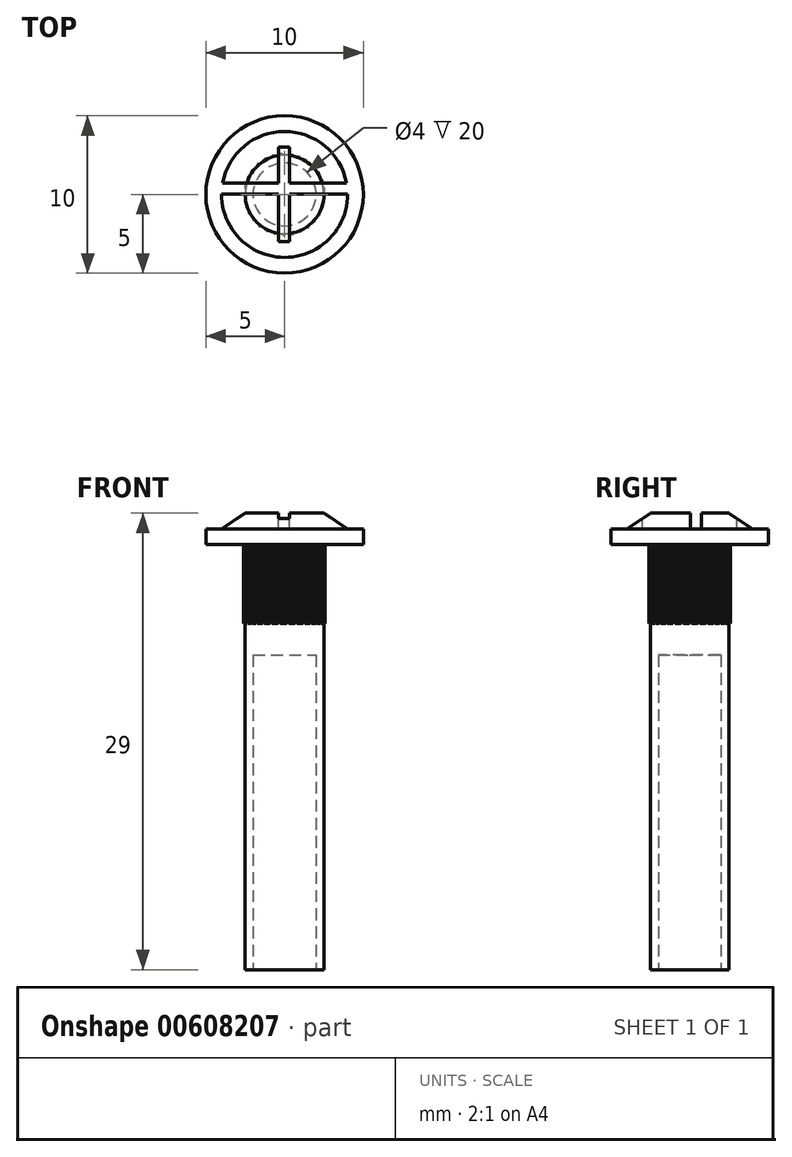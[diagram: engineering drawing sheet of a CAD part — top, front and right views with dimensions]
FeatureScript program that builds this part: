
annotation { "Feature Type Name" : "Feature", "Feature Type Description" : "" }
export const myFeature = defineFeature(function(context is Context, id is Id, definition is map)
    precondition{}
    {
        {
            var Q0;
            Q0=qCreatedBy(makeId("Front.planeOp"),FACE);
            var sketch = newSketch(context, id + "F0", { "sketchPlane" : qUnion([Q0])});
            skLineSegment(sketch, "E0.bottom", {"start": v(0, 12.5) * mm, "end": v(2.5, 12.5) * mm});
            skLineSegment(sketch, "E0.top", {"start": v(0, -14.5) * mm, "end": v(2.5, -14.5) * mm});
            skLineSegment(sketch, "E0.right", {"start": v(2.5, 12.5) * mm, "end": v(2.5, -14.5) * mm});
            skLineSegment(sketch, "E1", {"start": v(2.5, 14.5) * mm, "end": v(4, 13.5) * mm});
            skLineSegment(sketch, "E2", {"start": v(4, 13.5) * mm, "end": v(5, 13.5) * mm});
            skLineSegment(sketch, "E3", {"start": v(5, 13.5) * mm, "end": v(5, 12.5) * mm});
            skLineSegment(sketch, "E4", {"start": v(5, 12.5) * mm, "end": v(2.5, 12.5) * mm});
            skLineSegment(sketch, "E5", {"start": v(0, -14.5) * mm, "end": v(0, 14.5) * mm});
            skLineSegment(sketch, "E6", {"start": v(2.5, 14.5) * mm, "end": v(0, 14.5) * mm});
            skSolve(sketch);
        }
        {
            var Q0;
            Q0 = qSketchRegion(id + "F0", true);
            var Q1;
            Q1=sQuery(id+"F0.wireOp",EDGE,"E5");
            revolve(context, id + "F1", {"entities" : qUnion([Q0]), "axis" : qUnion([Q1]), "revolveType" : RevolveType.FULL});
        }
        {
            var Q0;
            Q0=makeQuery(id+"F1.opRevolve","SWEPT_FACE",FACE,{"disambiguationData":[OSD([sQuery(id+"F0.wireOp",EDGE,"E0.top")])]});
            var sketch = newSketch(context, id + "F2", { "sketchPlane" : qUnion([Q0])});
            skCircle(sketch, "E7", {"center": v(0, 0) * mm, "radius": 2 * mm});
            skSolve(sketch);
        }
        {
            var Q0;
            Q0 = qSketchRegion(id + "F2", true);
            extrude(context, id + "F3", {"entities" : qUnion([Q0]), "operationType" : NewBodyOperationType.REMOVE, "oppositeDirection" : true, "depth" : 20 * mm, "offsetDistance" : 25 * mm});
        }
        {
            var Q0;
            Q0=makeQuery(id+"F1.opRevolve","SWEPT_FACE",FACE,{"disambiguationData":[OSD([sQuery(id+"F0.wireOp",EDGE,"E6")])]});
            var sketch = newSketch(context, id + "F4", { "sketchPlane" : qUnion([Q0])});
            skLineSegment(sketch, "E8.bottom", {"start": v(-4, 0.73) * mm, "end": v(4, 0.73) * mm});
            skLineSegment(sketch, "E8.top", {"start": v(-4, 0.03) * mm, "end": v(4, 0.03) * mm});
            skLineSegment(sketch, "E8.left", {"start": v(-4, 0.73) * mm, "end": v(-4, 0.03) * mm});
            skLineSegment(sketch, "E8.right", {"start": v(4, 0.73) * mm, "end": v(4, 0.03) * mm});
            skLineSegment(sketch, "E9.bottom", {"start": v(-0.39, 3) * mm, "end": v(0.31, 3) * mm});
            skLineSegment(sketch, "E9.top", {"start": v(-0.39, -3) * mm, "end": v(0.31, -3) * mm});
            skLineSegment(sketch, "E9.left", {"start": v(-0.39, 3) * mm, "end": v(-0.39, -3) * mm});
            skLineSegment(sketch, "E9.right", {"start": v(0.31, 3) * mm, "end": v(0.31, -3) * mm});
            skSolve(sketch);
        }
        {
            var Q0;
            Q0 = qSketchRegion(id + "F4", true);
            extrude(context, id + "F5", {"entities" : qUnion([Q0]), "operationType" : NewBodyOperationType.REMOVE, "oppositeDirection" : true, "depth" : 1 * mm, "offsetDistance" : 25 * mm});
        }
        {
            var Q0;
            Q0=makeQuery(id+"F1.opRevolve","SWEPT_FACE",FACE,{"disambiguationData":[OSD([sQuery(id+"F0.wireOp",EDGE,"E4")])]});
            var sketch = newSketch(context, id + "F6", { "sketchPlane" : qUnion([Q0])});
            skLineSegment(sketch, "E10", {"start": v(-2.32, 0.94) * mm, "end": v(-2.32, 1.16) * mm});
            skLineSegment(sketch, "E11", {"start": v(-2.32, 1.16) * mm, "end": v(-2.14, 1.3) * mm});
            skLineSegment(sketch, "E12", {"start": v(-2.14, 1.3) * mm, "end": v(-2.32, 0.94) * mm});
            skLineSegment(sketch, "E13.1.0", {"start": v(-1.8, 1.72) * mm, "end": v(-2.06, 1.42) * mm});
            skLineSegment(sketch, "E13.1.1", {"start": v(-2.06, 1.42) * mm, "end": v(-2.01, 1.63) * mm});
            skLineSegment(sketch, "E13.1.2", {"start": v(-2.01, 1.63) * mm, "end": v(-1.8, 1.72) * mm});
            skLineSegment(sketch, "E13.2.0", {"start": v(-1.4, 2.07) * mm, "end": v(-1.7, 1.82) * mm});
            skLineSegment(sketch, "E13.2.1", {"start": v(-1.7, 1.82) * mm, "end": v(-1.62, 2.03) * mm});
            skLineSegment(sketch, "E13.2.2", {"start": v(-1.62, 2.03) * mm, "end": v(-1.4, 2.07) * mm});
            skLineSegment(sketch, "E13.3.0", {"start": v(-0.92, 2.32) * mm, "end": v(-1.28, 2.15) * mm});
            skLineSegment(sketch, "E13.3.1", {"start": v(-1.28, 2.15) * mm, "end": v(-1.14, 2.33) * mm});
            skLineSegment(sketch, "E13.3.2", {"start": v(-1.14, 2.33) * mm, "end": v(-0.92, 2.32) * mm});
            skLineSegment(sketch, "E13.4.0", {"start": v(-0.4, 2.47) * mm, "end": v(-0.79, 2.37) * mm});
            skLineSegment(sketch, "E13.4.1", {"start": v(-0.79, 2.37) * mm, "end": v(-0.62, 2.52) * mm});
            skLineSegment(sketch, "E13.4.2", {"start": v(-0.62, 2.52) * mm, "end": v(-0.4, 2.47) * mm});
            skLineSegment(sketch, "E13.5.0", {"start": v(0.14, 2.5) * mm, "end": v(-0.26, 2.49) * mm});
            skLineSegment(sketch, "E13.5.1", {"start": v(-0.26, 2.49) * mm, "end": v(-0.06, 2.6) * mm});
            skLineSegment(sketch, "E13.5.2", {"start": v(-0.06, 2.6) * mm, "end": v(0.14, 2.5) * mm});
            skLineSegment(sketch, "E13.6.0", {"start": v(0.67, 2.4) * mm, "end": v(0.28, 2.48) * mm});
            skLineSegment(sketch, "E13.6.1", {"start": v(0.28, 2.48) * mm, "end": v(0.5, 2.54) * mm});
            skLineSegment(sketch, "E13.6.2", {"start": v(0.5, 2.54) * mm, "end": v(0.67, 2.4) * mm});
            skLineSegment(sketch, "E13.7.0", {"start": v(1.17, 2.2) * mm, "end": v(0.8, 2.37) * mm});
            skLineSegment(sketch, "E13.7.1", {"start": v(0.8, 2.37) * mm, "end": v(1.03, 2.38) * mm});
            skLineSegment(sketch, "E13.7.2", {"start": v(1.03, 2.38) * mm, "end": v(1.17, 2.2) * mm});
            skLineSegment(sketch, "E13.8.0", {"start": v(1.62, 1.9) * mm, "end": v(1.3, 2.14) * mm});
            skLineSegment(sketch, "E13.8.1", {"start": v(1.3, 2.14) * mm, "end": v(1.51, 2.1) * mm});
            skLineSegment(sketch, "E13.8.2", {"start": v(1.51, 2.1) * mm, "end": v(1.62, 1.9) * mm});
            skLineSegment(sketch, "E13.9.0", {"start": v(1.99, 1.52) * mm, "end": v(1.72, 1.81) * mm});
            skLineSegment(sketch, "E13.9.1", {"start": v(1.72, 1.81) * mm, "end": v(1.93, 1.73) * mm});
            skLineSegment(sketch, "E13.9.2", {"start": v(1.93, 1.73) * mm, "end": v(1.99, 1.52) * mm});
            skLineSegment(sketch, "E13.10.0", {"start": v(2.27, 1.05) * mm, "end": v(2.07, 1.4) * mm});
            skLineSegment(sketch, "E13.10.1", {"start": v(2.07, 1.4) * mm, "end": v(2.26, 1.28) * mm});
            skLineSegment(sketch, "E13.10.2", {"start": v(2.26, 1.28) * mm, "end": v(2.27, 1.05) * mm});
            skLineSegment(sketch, "E13.11.0", {"start": v(2.44, 0.54) * mm, "end": v(2.32, 0.92) * mm});
            skLineSegment(sketch, "E13.11.1", {"start": v(2.32, 0.92) * mm, "end": v(2.48, 0.76) * mm});
            skLineSegment(sketch, "E13.11.2", {"start": v(2.48, 0.76) * mm, "end": v(2.44, 0.54) * mm});
            skLineSegment(sketch, "E13.12.0", {"start": v(2.5, 0) * mm, "end": v(2.47, 0.4) * mm});
            skLineSegment(sketch, "E13.12.1", {"start": v(2.47, 0.4) * mm, "end": v(2.58, 0.22) * mm});
            skLineSegment(sketch, "E13.12.2", {"start": v(2.58, 0.22) * mm, "end": v(2.5, 0) * mm});
            skLineSegment(sketch, "E13.13.0", {"start": v(2.44, -0.53) * mm, "end": v(2.5, -0.13) * mm});
            skLineSegment(sketch, "E13.13.1", {"start": v(2.5, -0.13) * mm, "end": v(2.57, -0.34) * mm});
            skLineSegment(sketch, "E13.13.2", {"start": v(2.57, -0.34) * mm, "end": v(2.44, -0.53) * mm});
            skLineSegment(sketch, "E13.14.0", {"start": v(2.27, -1.04) * mm, "end": v(2.4, -0.67) * mm});
            skLineSegment(sketch, "E13.14.1", {"start": v(2.4, -0.67) * mm, "end": v(2.44, -0.89) * mm});
            skLineSegment(sketch, "E13.14.2", {"start": v(2.44, -0.89) * mm, "end": v(2.27, -1.04) * mm});
            skLineSegment(sketch, "E13.15.0", {"start": v(2, -1.5) * mm, "end": v(2.21, -1.17) * mm});
            skLineSegment(sketch, "E13.15.1", {"start": v(2.21, -1.17) * mm, "end": v(2.19, -1.39) * mm});
            skLineSegment(sketch, "E13.15.2", {"start": v(2.19, -1.39) * mm, "end": v(2, -1.5) * mm});
            skLineSegment(sketch, "E13.16.0", {"start": v(1.63, -1.9) * mm, "end": v(1.9, -1.61) * mm});
            skLineSegment(sketch, "E13.16.1", {"start": v(1.9, -1.61) * mm, "end": v(1.84, -1.82) * mm});
            skLineSegment(sketch, "E13.16.2", {"start": v(1.84, -1.82) * mm, "end": v(1.63, -1.9) * mm});
            skLineSegment(sketch, "E13.17.0", {"start": v(1.19, -2.2) * mm, "end": v(1.52, -1.99) * mm});
            skLineSegment(sketch, "E13.17.1", {"start": v(1.52, -1.99) * mm, "end": v(1.4, -2.18) * mm});
            skLineSegment(sketch, "E13.17.2", {"start": v(1.4, -2.18) * mm, "end": v(1.19, -2.2) * mm});
            skLineSegment(sketch, "E13.18.0", {"start": v(0.69, -2.4) * mm, "end": v(1.06, -2.26) * mm});
            skLineSegment(sketch, "E13.18.1", {"start": v(1.06, -2.26) * mm, "end": v(0.9, -2.43) * mm});
            skLineSegment(sketch, "E13.18.2", {"start": v(0.9, -2.43) * mm, "end": v(0.69, -2.4) * mm});
            skLineSegment(sketch, "E13.19.0", {"start": v(0.15, -2.5) * mm, "end": v(0.55, -2.44) * mm});
            skLineSegment(sketch, "E13.19.1", {"start": v(0.55, -2.44) * mm, "end": v(0.37, -2.57) * mm});
            skLineSegment(sketch, "E13.19.2", {"start": v(0.37, -2.57) * mm, "end": v(0.15, -2.5) * mm});
            skLineSegment(sketch, "E13.20.0", {"start": v(-0.38, -2.47) * mm, "end": v(0.01, -2.5) * mm});
            skLineSegment(sketch, "E13.20.1", {"start": v(0.01, -2.5) * mm, "end": v(-0.2, -2.58) * mm});
            skLineSegment(sketch, "E13.20.2", {"start": v(-0.2, -2.58) * mm, "end": v(-0.38, -2.47) * mm});
            skLineSegment(sketch, "E13.21.0", {"start": v(-0.9, -2.33) * mm, "end": v(-0.52, -2.44) * mm});
            skLineSegment(sketch, "E13.21.1", {"start": v(-0.52, -2.44) * mm, "end": v(-0.74, -2.48) * mm});
            skLineSegment(sketch, "E13.21.2", {"start": v(-0.74, -2.48) * mm, "end": v(-0.9, -2.33) * mm});
            skLineSegment(sketch, "E13.22.0", {"start": v(-1.38, -2.08) * mm, "end": v(-1.04, -2.28) * mm});
            skLineSegment(sketch, "E13.22.1", {"start": v(-1.04, -2.28) * mm, "end": v(-1.26, -2.27) * mm});
            skLineSegment(sketch, "E13.22.2", {"start": v(-1.26, -2.27) * mm, "end": v(-1.38, -2.08) * mm});
            skLineSegment(sketch, "E13.23.0", {"start": v(-1.8, -1.74) * mm, "end": v(-1.5, -2) * mm});
            skLineSegment(sketch, "E13.23.1", {"start": v(-1.5, -2) * mm, "end": v(-1.71, -1.94) * mm});
            skLineSegment(sketch, "E13.23.2", {"start": v(-1.71, -1.94) * mm, "end": v(-1.8, -1.74) * mm});
            skLineSegment(sketch, "E13.24.0", {"start": v(-2.13, -1.31) * mm, "end": v(-1.9, -1.63) * mm});
            skLineSegment(sketch, "E13.24.1", {"start": v(-1.9, -1.63) * mm, "end": v(-2.1, -1.53) * mm});
            skLineSegment(sketch, "E13.24.2", {"start": v(-2.1, -1.53) * mm, "end": v(-2.13, -1.31) * mm});
            skLineSegment(sketch, "E13.25.0", {"start": v(-2.36, -0.82) * mm, "end": v(-2.2, -1.19) * mm});
            skLineSegment(sketch, "E13.25.1", {"start": v(-2.2, -1.19) * mm, "end": v(-2.37, -1.05) * mm});
            skLineSegment(sketch, "E13.25.2", {"start": v(-2.37, -1.05) * mm, "end": v(-2.36, -0.82) * mm});
            skLineSegment(sketch, "E13.26.0", {"start": v(-2.48, -0.3) * mm, "end": v(-2.4, -0.69) * mm});
            skLineSegment(sketch, "E13.26.1", {"start": v(-2.4, -0.69) * mm, "end": v(-2.54, -0.51) * mm});
            skLineSegment(sketch, "E13.26.2", {"start": v(-2.54, -0.51) * mm, "end": v(-2.48, -0.3) * mm});
            skLineSegment(sketch, "E13.27.0", {"start": v(-2.49, 0.24) * mm, "end": v(-2.5, -0.16) * mm});
            skLineSegment(sketch, "E13.27.1", {"start": v(-2.5, -0.16) * mm, "end": v(-2.6, 0.04) * mm});
            skLineSegment(sketch, "E13.27.2", {"start": v(-2.6, 0.04) * mm, "end": v(-2.49, 0.24) * mm});
            skLineSegment(sketch, "E13.28.0", {"start": v(-2.38, 0.77) * mm, "end": v(-2.47, 0.38) * mm});
            skLineSegment(sketch, "E13.28.1", {"start": v(-2.47, 0.38) * mm, "end": v(-2.52, 0.6) * mm});
            skLineSegment(sketch, "E13.28.2", {"start": v(-2.52, 0.6) * mm, "end": v(-2.38, 0.77) * mm});
            skLineSegment(sketch, "E13.29.0", {"start": v(-2.16, 1.26) * mm, "end": v(-2.33, 0.9) * mm});
            skLineSegment(sketch, "E13.29.1", {"start": v(-2.33, 0.9) * mm, "end": v(-2.34, 1.12) * mm});
            skLineSegment(sketch, "E13.29.2", {"start": v(-2.34, 1.12) * mm, "end": v(-2.16, 1.26) * mm});
            skPoint(sketch, "E13.center", {"position": v(0, 0) * mm});
            skLineSegment(sketch, "E13.anchor1", {"start": v(0, 0) * mm, "end": v(-2.32, 0.94) * mm, "construction": true});
            skLineSegment(sketch, "E13.anchor2", {"start": v(0, 0) * mm, "end": v(-2.33, 0.9) * mm, "construction": true});
            skSolve(sketch);
        }
        {
            var Q0;
            Q0 = qSketchRegion(id + "F6", true);
            extrude(context, id + "F7", {"entities" : qUnion([Q0]), "operationType" : NewBodyOperationType.ADD, "depth" : 5 * mm, "offsetDistance" : 25 * mm});
        }
    });
